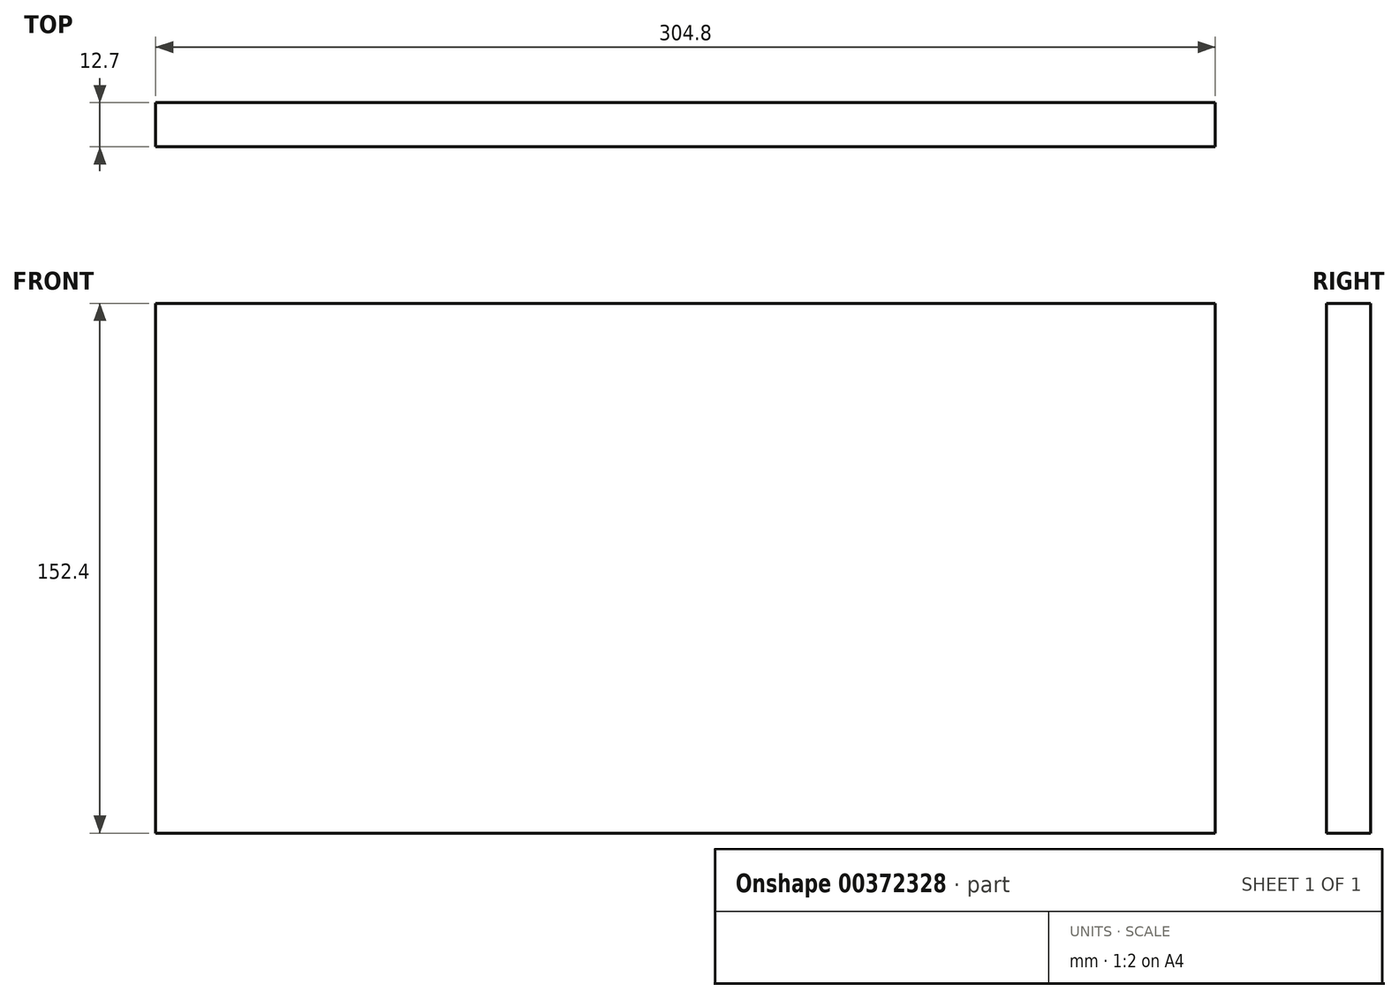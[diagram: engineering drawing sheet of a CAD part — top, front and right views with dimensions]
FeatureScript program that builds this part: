
annotation { "Feature Type Name" : "Feature", "Feature Type Description" : "" }
export const myFeature = defineFeature(function(context is Context, id is Id, definition is map)
    precondition{}
    {
        {
            var Q0;
            Q0=qCreatedBy(makeId("Front.planeOp"),FACE);
            var sketch = newSketch(context, id + "F0", { "sketchPlane" : qUnion([Q0])});
            skLineSegment(sketch, "E0.bottom", {"start": v(0, 0) * mm, "end": v(304.8, 0) * mm});
            skLineSegment(sketch, "E0.top", {"start": v(0, 152.4) * mm, "end": v(304.8, 152.4) * mm});
            skLineSegment(sketch, "E0.left", {"start": v(0, 0) * mm, "end": v(0, 152.4) * mm});
            skLineSegment(sketch, "E0.right", {"start": v(304.8, 0) * mm, "end": v(304.8, 152.4) * mm});
            skSolve(sketch);
        }
        {
            var Q0;
            Q0 = qSketchRegion(id + "F0", true);
            extrude(context, id + "F1", {"entities" : qUnion([Q0]), "depth" : 12.7 * mm});
        }
    });
